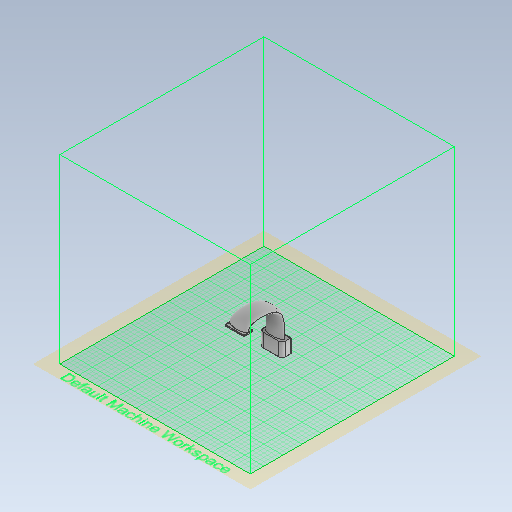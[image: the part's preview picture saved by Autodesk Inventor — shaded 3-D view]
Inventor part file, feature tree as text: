
AUTODESK INVENTOR PART (.ipt)
format: ipt  version: 2021 (Build 250183000, 183)  size: 738,816 bytes
history: native  units: mm
features: sketch x3, extrude x1, plane x1, sweep x1
ambient origin geometry x8: Origin, YZ Plane, XZ Plane, XY Plane, X Axis, Y Axis, Z Axis, Center Point
bodies: Volumenkörper1 (feature_tree)
feature tree (6):
  sketch  "Skizze1"  dims[d0=50.0mm d1=30.0mm]
  extrude  "Extrusion1"  Depth=30.0mm
  plane  "Arbeitsebene1"
  sweep  "Sweeping5"
  sketch  "Skizze8"  dims[d2=20.0mm d3=0.0mm d7=50.0mm]
  sketch  "Skizze9"  dims[d25=20.0mm d26=7.0mm d38=10.0mm d42=0.0mm d43=0.0mm]
